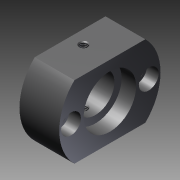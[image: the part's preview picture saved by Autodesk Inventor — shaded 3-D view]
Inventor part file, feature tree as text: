
AUTODESK INVENTOR PART (.ipt)
format: ipt  version: 2011 SP1 (Build 150282100, 282)  size: 156,672 bytes
history: native  units: mm
features: other x21, sketch x5, revolve x4, thread x3, extrude x1, pattern_linear x1
ambient origin geometry x8: Origin, YZ Plane, XZ Plane, XY Plane, X Axis, Y Axis, Z Axis, Center Point
bodies: Solid1 (feature_tree)
feature tree (35):
  revolve  "Revolution1"  [1 undecoded]
  extrude  "Extrusion1"  Depth=14.147mm TaperAngle=0.0deg
  revolve  "Revolution2"  Angle=360.0deg
  thread  "Thread1"  [1 undecoded]
  pattern_linear  "Rectangular Pattern1"  Spacing1=0.0mm  [1 undecoded]
  revolve  "Revolution3"  [1 undecoded]
  thread  "Thread2"  [1 undecoded]
  revolve  "Revolution4"  [1 undecoded]
  thread  "Thread3"  [1 undecoded]
  other  "to_bearings_XY"
  other  "to_bearings_YZ"
  other  "to_bearings_ZX"
  other  "to_bearings_X"
  other  "to_bearings_Y"
  other  "to_bearings_Z"
  other  "to_bearings_Center"
  other  "to_screw1_XY"
  other  "to_screw1_YZ"
  other  "to_screw1_ZX"
  other  "to_screw1_X"
  other  "to_screw1_Y"
  other  "to_screw1_Z"
  other  "to_screw1_Center"
  other  "to_screw2_XY"
  other  "to_screw2_YZ"
  other  "to_screw2_ZX"
  other  "to_screw2_X"
  other  "to_screw2_Y"
  other  "to_screw2_Z"
  other  "to_screw2_Center"
  sketch  "Sketch_1"  dims[d0=360.0deg d1=24.0mm d2=0.0mm]
  sketch  "Sketch_2"  dims[d3=360.0deg d4=14.147mm d5=0.0mm]
  sketch  "Sketch_3"  dims[d6=20.0mm d8=43.0mm d9=10.0mm d11=0.0mm d12=360.0deg d13=8.984mm d14=0.0mm]
  sketch  "Sketch_4"  dims[d15=360.0deg]
  sketch  "Sketch_6"  dims[d16=8.984mm d17=0.0mm d18=0.0mm]
note: 7 required parameter values undecoded (feature->parameter linkage not recoverable at this tier; creation-order binding heuristic only, values carry confidence <= 0.55)